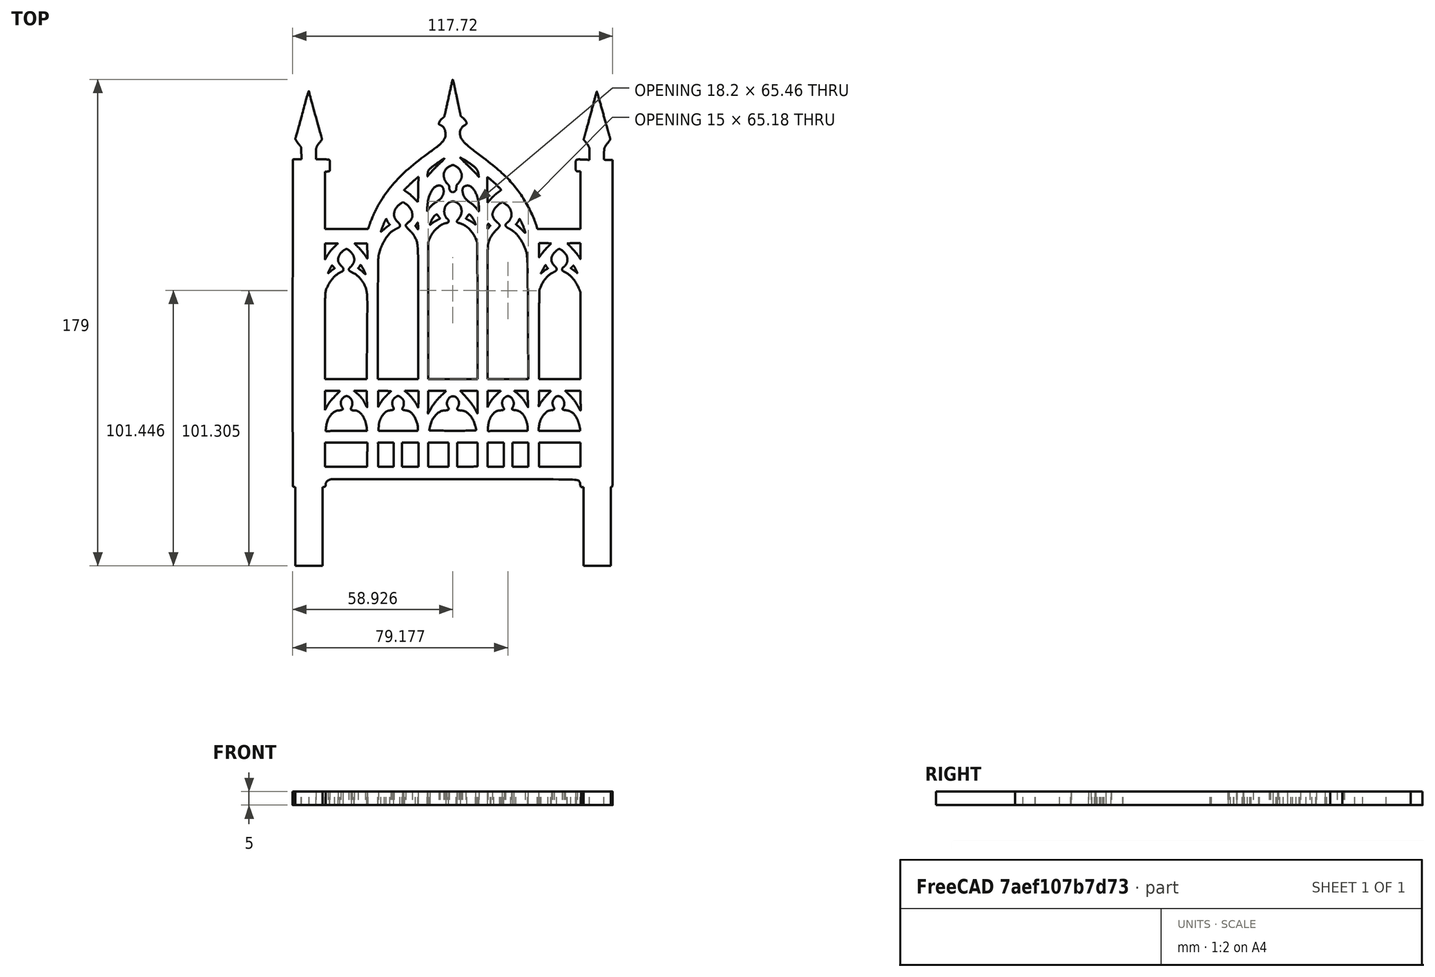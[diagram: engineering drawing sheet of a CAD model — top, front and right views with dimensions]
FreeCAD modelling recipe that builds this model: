
FCSTD DOCUMENT  (FreeCAD 1.0R1.0.1)
Label: Fence01_Flat
License: All rights reserved
LicenseURL: http://en.wikipedia.org/wiki/All_rights_reserved
objects: Part::Box×2, Sketcher::SketchObject×1, PartDesign::Pad×1, PartDesign::Body×1, Part::MultiFuse×1
note: 9 computed .brp shape members not serialized (recipe doc carries the construction recipe); baked Part::Feature solids carry a one-line shape summary decoded from their .brp

FEATURE [Sketcher::SketchObject] Sketch
  ArcFitTolerance = 1e-06
  AttachmentSupport = -> [XY_Plane]
  FullyConstrained = false
  MakeInternals = false
  MapMode = 5
  sketch-geometry (557):
    g0: BSplineCurve PolesCount=4 KnotsCount=2 Degree=3 IsPeriodic=0
    g1: BSplineCurve PolesCount=2 KnotsCount=2 Degree=1 IsPeriodic=0
    g2: BSplineCurve PolesCount=4 KnotsCount=2 Degree=3 IsPeriodic=0
    g3: BSplineCurve PolesCount=2 KnotsCount=2 Degree=1 IsPeriodic=0
    g4: BSplineCurve PolesCount=2 KnotsCount=2 Degree=1 IsPeriodic=0
    g5: BSplineCurve PolesCount=2 KnotsCount=2 Degree=1 IsPeriodic=0
    g6: BSplineCurve PolesCount=2 KnotsCount=2 Degree=1 IsPeriodic=0
    g7: BSplineCurve PolesCount=4 KnotsCount=2 Degree=3 IsPeriodic=0
    g8: BSplineCurve PolesCount=4 KnotsCount=2 Degree=3 IsPeriodic=0
    g9: BSplineCurve PolesCount=4 KnotsCount=2 Degree=3 IsPeriodic=0
    g10: BSplineCurve PolesCount=4 KnotsCount=2 Degree=3 IsPeriodic=0
    g11: BSplineCurve PolesCount=4 KnotsCount=2 Degree=3 IsPeriodic=0
    g12: BSplineCurve PolesCount=4 KnotsCount=2 Degree=3 IsPeriodic=0
    g13: BSplineCurve PolesCount=2 KnotsCount=2 Degree=1 IsPeriodic=0
    g14: BSplineCurve PolesCount=2 KnotsCount=2 Degree=1 IsPeriodic=0
    g15: BSplineCurve PolesCount=4 KnotsCount=2 Degree=3 IsPeriodic=0
    g16: BSplineCurve PolesCount=4 KnotsCount=2 Degree=3 IsPeriodic=0
    g17: BSplineCurve PolesCount=2 KnotsCount=2 Degree=1 IsPeriodic=0
    g18: BSplineCurve PolesCount=2 KnotsCount=2 Degree=1 IsPeriodic=0
    g19: BSplineCurve PolesCount=2 KnotsCount=2 Degree=1 IsPeriodic=0
    g20: BSplineCurve PolesCount=2 KnotsCount=2 Degree=1 IsPeriodic=0
    g21: BSplineCurve PolesCount=2 KnotsCount=2 Degree=1 IsPeriodic=0
    g22: BSplineCurve PolesCount=2 KnotsCount=2 Degree=1 IsPeriodic=0
    g23: BSplineCurve PolesCount=2 KnotsCount=2 Degree=1 IsPeriodic=0
    g24: BSplineCurve PolesCount=2 KnotsCount=2 Degree=1 IsPeriodic=0
    g25: BSplineCurve PolesCount=4 KnotsCount=2 Degree=3 IsPeriodic=0
    g26: BSplineCurve PolesCount=4 KnotsCount=2 Degree=3 IsPeriodic=0
    g27: BSplineCurve PolesCount=4 KnotsCount=2 Degree=3 IsPeriodic=0
    g28: BSplineCurve PolesCount=4 KnotsCount=2 Degree=3 IsPeriodic=0
    g29: BSplineCurve PolesCount=4 KnotsCount=2 Degree=3 IsPeriodic=0
    g30: BSplineCurve PolesCount=4 KnotsCount=2 Degree=3 IsPeriodic=0
    g31: BSplineCurve PolesCount=4 KnotsCount=2 Degree=3 IsPeriodic=0
    g32: BSplineCurve PolesCount=4 KnotsCount=2 Degree=3 IsPeriodic=0
    g33: BSplineCurve PolesCount=4 KnotsCount=2 Degree=3 IsPeriodic=0
    g34: BSplineCurve PolesCount=4 KnotsCount=2 Degree=3 IsPeriodic=0
    g35: BSplineCurve PolesCount=4 KnotsCount=2 Degree=3 IsPeriodic=0
    g36: BSplineCurve PolesCount=4 KnotsCount=2 Degree=3 IsPeriodic=0
    g37: BSplineCurve PolesCount=4 KnotsCount=2 Degree=3 IsPeriodic=0
    g38: BSplineCurve PolesCount=2 KnotsCount=2 Degree=1 IsPeriodic=0
    g39: BSplineCurve PolesCount=2 KnotsCount=2 Degree=1 IsPeriodic=0
    g40: BSplineCurve PolesCount=4 KnotsCount=2 Degree=3 IsPeriodic=0
    g41: BSplineCurve PolesCount=4 KnotsCount=2 Degree=3 IsPeriodic=0
    g42: BSplineCurve PolesCount=4 KnotsCount=2 Degree=3 IsPeriodic=0
    g43: BSplineCurve PolesCount=4 KnotsCount=2 Degree=3 IsPeriodic=0
    g44: BSplineCurve PolesCount=4 KnotsCount=2 Degree=3 IsPeriodic=0
    g45: BSplineCurve PolesCount=4 KnotsCount=2 Degree=3 IsPeriodic=0
    g46: BSplineCurve PolesCount=2 KnotsCount=2 Degree=1 IsPeriodic=0
    g47: BSplineCurve PolesCount=2 KnotsCount=2 Degree=1 IsPeriodic=0
    g48: BSplineCurve PolesCount=2 KnotsCount=2 Degree=1 IsPeriodic=0
    g49: BSplineCurve PolesCount=2 KnotsCount=2 Degree=1 IsPeriodic=0
    g50: BSplineCurve PolesCount=2 KnotsCount=2 Degree=1 IsPeriodic=0
    g51: BSplineCurve PolesCount=2 KnotsCount=2 Degree=1 IsPeriodic=0
    g52: BSplineCurve PolesCount=4 KnotsCount=2 Degree=3 IsPeriodic=0
    g53: BSplineCurve PolesCount=4 KnotsCount=2 Degree=3 IsPeriodic=0
    g54: BSplineCurve PolesCount=2 KnotsCount=2 Degree=1 IsPeriodic=0
    g55: BSplineCurve PolesCount=2 KnotsCount=2 Degree=1 IsPeriodic=0
    g56: BSplineCurve PolesCount=4 KnotsCount=2 Degree=3 IsPeriodic=0
    g57: BSplineCurve PolesCount=2 KnotsCount=2 Degree=1 IsPeriodic=0
    g58: BSplineCurve PolesCount=2 KnotsCount=2 Degree=1 IsPeriodic=0
    g59: BSplineCurve PolesCount=4 KnotsCount=2 Degree=3 IsPeriodic=0
    g60: BSplineCurve PolesCount=4 KnotsCount=2 Degree=3 IsPeriodic=0
    g61: BSplineCurve PolesCount=4 KnotsCount=2 Degree=3 IsPeriodic=0
    g62: BSplineCurve PolesCount=4 KnotsCount=2 Degree=3 IsPeriodic=0
    g63: BSplineCurve PolesCount=4 KnotsCount=2 Degree=3 IsPeriodic=0
    g64: BSplineCurve PolesCount=4 KnotsCount=2 Degree=3 IsPeriodic=0
    g65: BSplineCurve PolesCount=4 KnotsCount=2 Degree=3 IsPeriodic=0
    g66: BSplineCurve PolesCount=2 KnotsCount=2 Degree=1 IsPeriodic=0
    g67: BSplineCurve PolesCount=2 KnotsCount=2 Degree=1 IsPeriodic=0
    g68: BSplineCurve PolesCount=4 KnotsCount=2 Degree=3 IsPeriodic=0
    g69: BSplineCurve PolesCount=2 KnotsCount=2 Degree=1 IsPeriodic=0
    g70: BSplineCurve PolesCount=4 KnotsCount=2 Degree=3 IsPeriodic=0
    g71: BSplineCurve PolesCount=4 KnotsCount=2 Degree=3 IsPeriodic=0
    g72: BSplineCurve PolesCount=2 KnotsCount=2 Degree=1 IsPeriodic=0
    g73: BSplineCurve PolesCount=2 KnotsCount=2 Degree=1 IsPeriodic=0
    g74: BSplineCurve PolesCount=4 KnotsCount=2 Degree=3 IsPeriodic=0
    g75: BSplineCurve PolesCount=4 KnotsCount=2 Degree=3 IsPeriodic=0
    g76: BSplineCurve PolesCount=4 KnotsCount=2 Degree=3 IsPeriodic=0
    g77: BSplineCurve PolesCount=4 KnotsCount=2 Degree=3 IsPeriodic=0
    g78: BSplineCurve PolesCount=4 KnotsCount=2 Degree=3 IsPeriodic=0
    g79: BSplineCurve PolesCount=4 KnotsCount=2 Degree=3 IsPeriodic=0
    g80: BSplineCurve PolesCount=4 KnotsCount=2 Degree=3 IsPeriodic=0
    g81: BSplineCurve PolesCount=4 KnotsCount=2 Degree=3 IsPeriodic=0
    g82: BSplineCurve PolesCount=2 KnotsCount=2 Degree=1 IsPeriodic=0
    g83: BSplineCurve PolesCount=2 KnotsCount=2 Degree=1 IsPeriodic=0
    g84: BSplineCurve PolesCount=2 KnotsCount=2 Degree=1 IsPeriodic=0
    g85: BSplineCurve PolesCount=2 KnotsCount=2 Degree=1 IsPeriodic=0
    g86: BSplineCurve PolesCount=2 KnotsCount=2 Degree=1 IsPeriodic=0
    g87: BSplineCurve PolesCount=2 KnotsCount=2 Degree=1 IsPeriodic=0
    g88: BSplineCurve PolesCount=2 KnotsCount=2 Degree=1 IsPeriodic=0
    g89: BSplineCurve PolesCount=2 KnotsCount=2 Degree=1 IsPeriodic=0
    g90: BSplineCurve PolesCount=2 KnotsCount=2 Degree=1 IsPeriodic=0
    g91: BSplineCurve PolesCount=2 KnotsCount=2 Degree=1 IsPeriodic=0
    g92: BSplineCurve PolesCount=2 KnotsCount=2 Degree=1 IsPeriodic=0
    g93: BSplineCurve PolesCount=2 KnotsCount=2 Degree=1 IsPeriodic=0
    g94: BSplineCurve PolesCount=2 KnotsCount=2 Degree=1 IsPeriodic=0
    g95: BSplineCurve PolesCount=2 KnotsCount=2 Degree=1 IsPeriodic=0
    g96: BSplineCurve PolesCount=2 KnotsCount=2 Degree=1 IsPeriodic=0
    g97: BSplineCurve PolesCount=2 KnotsCount=2 Degree=1 IsPeriodic=0
    g98: BSplineCurve PolesCount=2 KnotsCount=2 Degree=1 IsPeriodic=0
    g99: BSplineCurve PolesCount=2 KnotsCount=2 Degree=1 IsPeriodic=0
    g100: BSplineCurve PolesCount=2 KnotsCount=2 Degree=1 IsPeriodic=0
    g101: BSplineCurve PolesCount=2 KnotsCount=2 Degree=1 IsPeriodic=0
    g102: BSplineCurve PolesCount=2 KnotsCount=2 Degree=1 IsPeriodic=0
    g103: BSplineCurve PolesCount=2 KnotsCount=2 Degree=1 IsPeriodic=0
    g104: BSplineCurve PolesCount=2 KnotsCount=2 Degree=1 IsPeriodic=0
    g105: BSplineCurve PolesCount=2 KnotsCount=2 Degree=1 IsPeriodic=0
    g106: BSplineCurve PolesCount=2 KnotsCount=2 Degree=1 IsPeriodic=0
    g107: BSplineCurve PolesCount=2 KnotsCount=2 Degree=1 IsPeriodic=0
    g108: BSplineCurve PolesCount=2 KnotsCount=2 Degree=1 IsPeriodic=0
    g109: BSplineCurve PolesCount=2 KnotsCount=2 Degree=1 IsPeriodic=0
    g110: BSplineCurve PolesCount=2 KnotsCount=2 Degree=1 IsPeriodic=0
    g111: BSplineCurve PolesCount=2 KnotsCount=2 Degree=1 IsPeriodic=0
    g112: BSplineCurve PolesCount=2 KnotsCount=2 Degree=1 IsPeriodic=0
    g113: BSplineCurve PolesCount=2 KnotsCount=2 Degree=1 IsPeriodic=0
    g114: BSplineCurve PolesCount=2 KnotsCount=2 Degree=1 IsPeriodic=0
    g115: BSplineCurve PolesCount=4 KnotsCount=2 Degree=3 IsPeriodic=0
    g116: BSplineCurve PolesCount=2 KnotsCount=2 Degree=1 IsPeriodic=0
    g117: BSplineCurve PolesCount=2 KnotsCount=2 Degree=1 IsPeriodic=0
    g118: BSplineCurve PolesCount=2 KnotsCount=2 Degree=1 IsPeriodic=0
    g119: BSplineCurve PolesCount=2 KnotsCount=2 Degree=1 IsPeriodic=0
    g120: BSplineCurve PolesCount=2 KnotsCount=2 Degree=1 IsPeriodic=0
    g121: BSplineCurve PolesCount=2 KnotsCount=2 Degree=1 IsPeriodic=0
    g122: BSplineCurve PolesCount=4 KnotsCount=2 Degree=3 IsPeriodic=0
    g123: BSplineCurve PolesCount=2 KnotsCount=2 Degree=1 IsPeriodic=0
    g124: BSplineCurve PolesCount=2 KnotsCount=2 Degree=1 IsPeriodic=0
    g125: BSplineCurve PolesCount=2 KnotsCount=2 Degree=1 IsPeriodic=0
    g126: BSplineCurve PolesCount=2 KnotsCount=2 Degree=1 IsPeriodic=0
    g127: BSplineCurve PolesCount=2 KnotsCount=2 Degree=1 IsPeriodic=0
    g128: BSplineCurve PolesCount=2 KnotsCount=2 Degree=1 IsPeriodic=0
    g129: BSplineCurve PolesCount=2 KnotsCount=2 Degree=1 IsPeriodic=0
    g130: BSplineCurve PolesCount=2 KnotsCount=2 Degree=1 IsPeriodic=0
    g131: BSplineCurve PolesCount=2 KnotsCount=2 Degree=1 IsPeriodic=0
    g132: BSplineCurve PolesCount=2 KnotsCount=2 Degree=1 IsPeriodic=0
    g133: BSplineCurve PolesCount=2 KnotsCount=2 Degree=1 IsPeriodic=0
    g134: BSplineCurve PolesCount=2 KnotsCount=2 Degree=1 IsPeriodic=0
    g135: BSplineCurve PolesCount=2 KnotsCount=2 Degree=1 IsPeriodic=0
    g136: BSplineCurve PolesCount=2 KnotsCount=2 Degree=1 IsPeriodic=0
    g137: BSplineCurve PolesCount=2 KnotsCount=2 Degree=1 IsPeriodic=0
    g138: BSplineCurve PolesCount=2 KnotsCount=2 Degree=1 IsPeriodic=0
    g139: BSplineCurve PolesCount=2 KnotsCount=2 Degree=1 IsPeriodic=0
    g140: BSplineCurve PolesCount=2 KnotsCount=2 Degree=1 IsPeriodic=0
    g141: BSplineCurve PolesCount=2 KnotsCount=2 Degree=1 IsPeriodic=0
    g142: BSplineCurve PolesCount=2 KnotsCount=2 Degree=1 IsPeriodic=0
    g143: BSplineCurve PolesCount=2 KnotsCount=2 Degree=1 IsPeriodic=0
    g144: BSplineCurve PolesCount=2 KnotsCount=2 Degree=1 IsPeriodic=0
    g145: BSplineCurve PolesCount=2 KnotsCount=2 Degree=1 IsPeriodic=0
    g146: BSplineCurve PolesCount=2 KnotsCount=2 Degree=1 IsPeriodic=0
    g147: BSplineCurve PolesCount=2 KnotsCount=2 Degree=1 IsPeriodic=0
    g148: BSplineCurve PolesCount=2 KnotsCount=2 Degree=1 IsPeriodic=0
    g149: BSplineCurve PolesCount=4 KnotsCount=2 Degree=3 IsPeriodic=0
    g150: BSplineCurve PolesCount=4 KnotsCount=2 Degree=3 IsPeriodic=0
    g151: BSplineCurve PolesCount=4 KnotsCount=2 Degree=3 IsPeriodic=0
    g152: BSplineCurve PolesCount=4 KnotsCount=2 Degree=3 IsPeriodic=0
    g153: BSplineCurve PolesCount=4 KnotsCount=2 Degree=3 IsPeriodic=0
    g154: BSplineCurve PolesCount=4 KnotsCount=2 Degree=3 IsPeriodic=0
    g155: BSplineCurve PolesCount=4 KnotsCount=2 Degree=3 IsPeriodic=0
    g156: BSplineCurve PolesCount=4 KnotsCount=2 Degree=3 IsPeriodic=0
    g157: BSplineCurve PolesCount=4 KnotsCount=2 Degree=3 IsPeriodic=0
    g158: BSplineCurve PolesCount=2 KnotsCount=2 Degree=1 IsPeriodic=0
    g159: BSplineCurve PolesCount=2 KnotsCount=2 Degree=1 IsPeriodic=0
    g160: BSplineCurve PolesCount=4 KnotsCount=2 Degree=3 IsPeriodic=0
    g161: BSplineCurve PolesCount=2 KnotsCount=2 Degree=1 IsPeriodic=0
    g162: BSplineCurve PolesCount=4 KnotsCount=2 Degree=3 IsPeriodic=0
    g163: BSplineCurve PolesCount=4 KnotsCount=2 Degree=3 IsPeriodic=0
    g164: BSplineCurve PolesCount=4 KnotsCount=2 Degree=3 IsPeriodic=0
    g165: BSplineCurve PolesCount=4 KnotsCount=2 Degree=3 IsPeriodic=0
    g166: BSplineCurve PolesCount=4 KnotsCount=2 Degree=3 IsPeriodic=0
    g167: BSplineCurve PolesCount=4 KnotsCount=2 Degree=3 IsPeriodic=0
    g168: BSplineCurve PolesCount=4 KnotsCount=2 Degree=3 IsPeriodic=0
    g169: BSplineCurve PolesCount=4 KnotsCount=2 Degree=3 IsPeriodic=0
    g170: BSplineCurve PolesCount=4 KnotsCount=2 Degree=3 IsPeriodic=0
    g171: BSplineCurve PolesCount=4 KnotsCount=2 Degree=3 IsPeriodic=0
    g172: BSplineCurve PolesCount=4 KnotsCount=2 Degree=3 IsPeriodic=0
    g173: BSplineCurve PolesCount=4 KnotsCount=2 Degree=3 IsPeriodic=0
    g174: BSplineCurve PolesCount=4 KnotsCount=2 Degree=3 IsPeriodic=0
    g175: BSplineCurve PolesCount=4 KnotsCount=2 Degree=3 IsPeriodic=0
    g176: BSplineCurve PolesCount=2 KnotsCount=2 Degree=1 IsPeriodic=0
    g177: BSplineCurve PolesCount=2 KnotsCount=2 Degree=1 IsPeriodic=0
    g178: BSplineCurve PolesCount=2 KnotsCount=2 Degree=1 IsPeriodic=0
    g179: BSplineCurve PolesCount=2 KnotsCount=2 Degree=1 IsPeriodic=0
    g180: BSplineCurve PolesCount=4 KnotsCount=2 Degree=3 IsPeriodic=0
    g181: BSplineCurve PolesCount=4 KnotsCount=2 Degree=3 IsPeriodic=0
    g182: BSplineCurve PolesCount=4 KnotsCount=2 Degree=3 IsPeriodic=0
    g183: BSplineCurve PolesCount=4 KnotsCount=2 Degree=3 IsPeriodic=0
    g184: BSplineCurve PolesCount=4 KnotsCount=2 Degree=3 IsPeriodic=0
    g185: BSplineCurve PolesCount=4 KnotsCount=2 Degree=3 IsPeriodic=0
    g186: BSplineCurve PolesCount=4 KnotsCount=2 Degree=3 IsPeriodic=0
    g187: BSplineCurve PolesCount=4 KnotsCount=2 Degree=3 IsPeriodic=0
    g188: BSplineCurve PolesCount=4 KnotsCount=2 Degree=3 IsPeriodic=0
    g189: BSplineCurve PolesCount=4 KnotsCount=2 Degree=3 IsPeriodic=0
    g190: BSplineCurve PolesCount=4 KnotsCount=2 Degree=3 IsPeriodic=0
    g191: BSplineCurve PolesCount=4 KnotsCount=2 Degree=3 IsPeriodic=0
    g192: BSplineCurve PolesCount=4 KnotsCount=2 Degree=3 IsPeriodic=0
    g193: BSplineCurve PolesCount=2 KnotsCount=2 Degree=1 IsPeriodic=0
    g194: BSplineCurve PolesCount=4 KnotsCount=2 Degree=3 IsPeriodic=0
    g195: BSplineCurve PolesCount=4 KnotsCount=2 Degree=3 IsPeriodic=0
    g196: BSplineCurve PolesCount=4 KnotsCount=2 Degree=3 IsPeriodic=0
    g197: BSplineCurve PolesCount=4 KnotsCount=2 Degree=3 IsPeriodic=0
    g198: BSplineCurve PolesCount=4 KnotsCount=2 Degree=3 IsPeriodic=0
    g199: BSplineCurve PolesCount=4 KnotsCount=2 Degree=3 IsPeriodic=0
    g200: BSplineCurve PolesCount=4 KnotsCount=2 Degree=3 IsPeriodic=0
    g201: BSplineCurve PolesCount=4 KnotsCount=2 Degree=3 IsPeriodic=0
    g202: BSplineCurve PolesCount=4 KnotsCount=2 Degree=3 IsPeriodic=0
    g203: BSplineCurve PolesCount=4 KnotsCount=2 Degree=3 IsPeriodic=0
    g204: BSplineCurve PolesCount=4 KnotsCount=2 Degree=3 IsPeriodic=0
    g205: BSplineCurve PolesCount=4 KnotsCount=2 Degree=3 IsPeriodic=0
    g206: BSplineCurve PolesCount=4 KnotsCount=2 Degree=3 IsPeriodic=0
    g207: BSplineCurve PolesCount=4 KnotsCount=2 Degree=3 IsPeriodic=0
    g208: BSplineCurve PolesCount=4 KnotsCount=2 Degree=3 IsPeriodic=0
    g209: BSplineCurve PolesCount=4 KnotsCount=2 Degree=3 IsPeriodic=0
    g210: BSplineCurve PolesCount=4 KnotsCount=2 Degree=3 IsPeriodic=0
    g211: BSplineCurve PolesCount=4 KnotsCount=2 Degree=3 IsPeriodic=0
    g212: BSplineCurve PolesCount=4 KnotsCount=2 Degree=3 IsPeriodic=0
    g213: BSplineCurve PolesCount=4 KnotsCount=2 Degree=3 IsPeriodic=0
    g214: BSplineCurve PolesCount=4 KnotsCount=2 Degree=3 IsPeriodic=0
    g215: BSplineCurve PolesCount=4 KnotsCount=2 Degree=3 IsPeriodic=0
    g216: BSplineCurve PolesCount=2 KnotsCount=2 Degree=1 IsPeriodic=0
    g217: BSplineCurve PolesCount=2 KnotsCount=2 Degree=1 IsPeriodic=0
    g218: BSplineCurve PolesCount=2 KnotsCount=2 Degree=1 IsPeriodic=0
    g219: BSplineCurve PolesCount=2 KnotsCount=2 Degree=1 IsPeriodic=0
    g220: BSplineCurve PolesCount=4 KnotsCount=2 Degree=3 IsPeriodic=0
    g221: BSplineCurve PolesCount=2 KnotsCount=2 Degree=1 IsPeriodic=0
    g222: BSplineCurve PolesCount=2 KnotsCount=2 Degree=1 IsPeriodic=0
    g223: BSplineCurve PolesCount=2 KnotsCount=2 Degree=1 IsPeriodic=0
    g224: BSplineCurve PolesCount=2 KnotsCount=2 Degree=1 IsPeriodic=0
    g225: BSplineCurve PolesCount=4 KnotsCount=2 Degree=3 IsPeriodic=0
    g226: BSplineCurve PolesCount=4 KnotsCount=2 Degree=3 IsPeriodic=0
    g227: BSplineCurve PolesCount=4 KnotsCount=2 Degree=3 IsPeriodic=0
    g228: BSplineCurve PolesCount=2 KnotsCount=2 Degree=1 IsPeriodic=0
    g229: BSplineCurve PolesCount=2 KnotsCount=2 Degree=1 IsPeriodic=0
    g230: BSplineCurve PolesCount=2 KnotsCount=2 Degree=1 IsPeriodic=0
    g231: BSplineCurve PolesCount=4 KnotsCount=2 Degree=3 IsPeriodic=0
    g232: BSplineCurve PolesCount=4 KnotsCount=2 Degree=3 IsPeriodic=0
    g233: BSplineCurve PolesCount=4 KnotsCount=2 Degree=3 IsPeriodic=0
    g234: BSplineCurve PolesCount=4 KnotsCount=2 Degree=3 IsPeriodic=0
    g235: BSplineCurve PolesCount=4 KnotsCount=2 Degree=3 IsPeriodic=0
    g236: BSplineCurve PolesCount=2 KnotsCount=2 Degree=1 IsPeriodic=0
    g237: BSplineCurve PolesCount=2 KnotsCount=2 Degree=1 IsPeriodic=0
    g238: BSplineCurve PolesCount=2 KnotsCount=2 Degree=1 IsPeriodic=0
    g239: BSplineCurve PolesCount=4 KnotsCount=2 Degree=3 IsPeriodic=0
    g240: BSplineCurve PolesCount=4 KnotsCount=2 Degree=3 IsPeriodic=0
    g241: BSplineCurve PolesCount=4 KnotsCount=2 Degree=3 IsPeriodic=0
    g242: BSplineCurve PolesCount=4 KnotsCount=2 Degree=3 IsPeriodic=0
    g243: BSplineCurve PolesCount=4 KnotsCount=2 Degree=3 IsPeriodic=0
    g244: BSplineCurve PolesCount=2 KnotsCount=2 Degree=1 IsPeriodic=0
    g245: BSplineCurve PolesCount=4 KnotsCount=2 Degree=3 IsPeriodic=0
    g246: BSplineCurve PolesCount=2 KnotsCount=2 Degree=1 IsPeriodic=0
    g247: BSplineCurve PolesCount=2 KnotsCount=2 Degree=1 IsPeriodic=0
    g248: BSplineCurve PolesCount=2 KnotsCount=2 Degree=1 IsPeriodic=0
    g249: BSplineCurve PolesCount=2 KnotsCount=2 Degree=1 IsPeriodic=0
    g250: BSplineCurve PolesCount=2 KnotsCount=2 Degree=1 IsPeriodic=0
    g251: BSplineCurve PolesCount=2 KnotsCount=2 Degree=1 IsPeriodic=0
    g252: BSplineCurve PolesCount=4 KnotsCount=2 Degree=3 IsPeriodic=0
    g253: BSplineCurve PolesCount=2 KnotsCount=2 Degree=1 IsPeriodic=0
    g254: BSplineCurve PolesCount=2 KnotsCount=2 Degree=1 IsPeriodic=0
    g255: BSplineCurve PolesCount=2 KnotsCount=2 Degree=1 IsPeriodic=0
    g256: BSplineCurve PolesCount=2 KnotsCount=2 Degree=1 IsPeriodic=0
    g257: BSplineCurve PolesCount=2 KnotsCount=2 Degree=1 IsPeriodic=0
    g258: BSplineCurve PolesCount=4 KnotsCount=2 Degree=3 IsPeriodic=0
    g259: BSplineCurve PolesCount=4 KnotsCount=2 Degree=3 IsPeriodic=0
    g260: BSplineCurve PolesCount=4 KnotsCount=2 Degree=3 IsPeriodic=0
    g261: BSplineCurve PolesCount=2 KnotsCount=2 Degree=1 IsPeriodic=0
    g262: BSplineCurve PolesCount=4 KnotsCount=2 Degree=3 IsPeriodic=0
    g263: BSplineCurve PolesCount=2 KnotsCount=2 Degree=1 IsPeriodic=0
    g264: BSplineCurve PolesCount=2 KnotsCount=2 Degree=1 IsPeriodic=0
    g265: BSplineCurve PolesCount=2 KnotsCount=2 Degree=1 IsPeriodic=0
    g266: BSplineCurve PolesCount=2 KnotsCount=2 Degree=1 IsPeriodic=0
    g267: BSplineCurve PolesCount=4 KnotsCount=2 Degree=3 IsPeriodic=0
    g268: BSplineCurve PolesCount=4 KnotsCount=2 Degree=3 IsPeriodic=0
    g269: BSplineCurve PolesCount=4 KnotsCount=2 Degree=3 IsPeriodic=0
    g270: BSplineCurve PolesCount=4 KnotsCount=2 Degree=3 IsPeriodic=0
    g271: BSplineCurve PolesCount=2 KnotsCount=2 Degree=1 IsPeriodic=0
    g272: BSplineCurve PolesCount=4 KnotsCount=2 Degree=3 IsPeriodic=0
    g273: BSplineCurve PolesCount=2 KnotsCount=2 Degree=1 IsPeriodic=0
    g274: BSplineCurve PolesCount=2 KnotsCount=2 Degree=1 IsPeriodic=0
    g275: BSplineCurve PolesCount=2 KnotsCount=2 Degree=1 IsPeriodic=0
    g276: BSplineCurve PolesCount=2 KnotsCount=2 Degree=1 IsPeriodic=0
    g277: BSplineCurve PolesCount=2 KnotsCount=2 Degree=1 IsPeriodic=0
    g278: BSplineCurve PolesCount=2 KnotsCount=2 Degree=1 IsPeriodic=0
    g279: BSplineCurve PolesCount=4 KnotsCount=2 Degree=3 IsPeriodic=0
    g280: BSplineCurve PolesCount=2 KnotsCount=2 Degree=1 IsPeriodic=0
    g281: BSplineCurve PolesCount=4 KnotsCount=2 Degree=3 IsPeriodic=0
    g282: BSplineCurve PolesCount=2 KnotsCount=2 Degree=1 IsPeriodic=0
    g283: BSplineCurve PolesCount=2 KnotsCount=2 Degree=1 IsPeriodic=0
    g284: BSplineCurve PolesCount=2 KnotsCount=2 Degree=1 IsPeriodic=0
    g285: BSplineCurve PolesCount=2 KnotsCount=2 Degree=1 IsPeriodic=0
    g286: BSplineCurve PolesCount=4 KnotsCount=2 Degree=3 IsPeriodic=0
    g287: BSplineCurve PolesCount=4 KnotsCount=2 Degree=3 IsPeriodic=0
    g288: BSplineCurve PolesCount=4 KnotsCount=2 Degree=3 IsPeriodic=0
    g289: BSplineCurve PolesCount=2 KnotsCount=2 Degree=1 IsPeriodic=0
    g290: BSplineCurve PolesCount=4 KnotsCount=2 Degree=3 IsPeriodic=0
    g291: BSplineCurve PolesCount=4 KnotsCount=2 Degree=3 IsPeriodic=0
    g292: BSplineCurve PolesCount=4 KnotsCount=2 Degree=3 IsPeriodic=0
    g293: BSplineCurve PolesCount=2 KnotsCount=2 Degree=1 IsPeriodic=0
    g294: BSplineCurve PolesCount=2 KnotsCount=2 Degree=1 IsPeriodic=0
    g295: BSplineCurve PolesCount=2 KnotsCount=2 Degree=1 IsPeriodic=0
    g296: BSplineCurve PolesCount=2 KnotsCount=2 Degree=1 IsPeriodic=0
    g297: BSplineCurve PolesCount=4 KnotsCount=2 Degree=3 IsPeriodic=0
    g298: BSplineCurve PolesCount=2 KnotsCount=2 Degree=1 IsPeriodic=0
    g299: BSplineCurve PolesCount=4 KnotsCount=2 Degree=3 IsPeriodic=0
    g300: BSplineCurve PolesCount=2 KnotsCount=2 Degree=1 IsPeriodic=0
    g301: BSplineCurve PolesCount=2 KnotsCount=2 Degree=1 IsPeriodic=0
    g302: BSplineCurve PolesCount=2 KnotsCount=2 Degree=1 IsPeriodic=0
    g303: BSplineCurve PolesCount=2 KnotsCount=2 Degree=1 IsPeriodic=0
    g304: BSplineCurve PolesCount=4 KnotsCount=2 Degree=3 IsPeriodic=0
    g305: BSplineCurve PolesCount=4 KnotsCount=2 Degree=3 IsPeriodic=0
    g306: BSplineCurve PolesCount=4 KnotsCount=2 Degree=3 IsPeriodic=0
    g307: BSplineCurve PolesCount=2 KnotsCount=2 Degree=1 IsPeriodic=0
    g308: BSplineCurve PolesCount=4 KnotsCount=2 Degree=3 IsPeriodic=0
    g309: BSplineCurve PolesCount=4 KnotsCount=2 Degree=3 IsPeriodic=0
    g310: BSplineCurve PolesCount=4 KnotsCount=2 Degree=3 IsPeriodic=0
    g311: BSplineCurve PolesCount=4 KnotsCount=2 Degree=3 IsPeriodic=0
    g312: BSplineCurve PolesCount=4 KnotsCount=2 Degree=3 IsPeriodic=0
    g313: BSplineCurve PolesCount=4 KnotsCount=2 Degree=3 IsPeriodic=0
    g314: BSplineCurve PolesCount=4 KnotsCount=2 Degree=3 IsPeriodic=0
    g315: BSplineCurve PolesCount=4 KnotsCount=2 Degree=3 IsPeriodic=0
    g316: BSplineCurve PolesCount=4 KnotsCount=2 Degree=3 IsPeriodic=0
    g317: BSplineCurve PolesCount=4 KnotsCount=2 Degree=3 IsPeriodic=0
    g318: BSplineCurve PolesCount=4 KnotsCount=2 Degree=3 IsPeriodic=0
    g319: BSplineCurve PolesCount=4 KnotsCount=2 Degree=3 IsPeriodic=0
    g320: BSplineCurve PolesCount=4 KnotsCount=2 Degree=3 IsPeriodic=0
    g321: BSplineCurve PolesCount=2 KnotsCount=2 Degree=1 IsPeriodic=0
    g322: BSplineCurve PolesCount=2 KnotsCount=2 Degree=1 IsPeriodic=0
    g323: BSplineCurve PolesCount=2 KnotsCount=2 Degree=1 IsPeriodic=0
    g324: BSplineCurve PolesCount=2 KnotsCount=2 Degree=1 IsPeriodic=0
    g325: BSplineCurve PolesCount=4 KnotsCount=2 Degree=3 IsPeriodic=0
    g326: BSplineCurve PolesCount=4 KnotsCount=2 Degree=3 IsPeriodic=0
    g327: BSplineCurve PolesCount=4 KnotsCount=2 Degree=3 IsPeriodic=0
    g328: BSplineCurve PolesCount=4 KnotsCount=2 Degree=3 IsPeriodic=0
    g329: BSplineCurve PolesCount=4 KnotsCount=2 Degree=3 IsPeriodic=0
    g330: BSplineCurve PolesCount=2 KnotsCount=2 Degree=1 IsPeriodic=0
    g331: BSplineCurve PolesCount=2 KnotsCount=2 Degree=1 IsPeriodic=0
    g332: BSplineCurve PolesCount=4 KnotsCount=2 Degree=3 IsPeriodic=0
    g333: BSplineCurve PolesCount=4 KnotsCount=2 Degree=3 IsPeriodic=0
    g334: BSplineCurve PolesCount=4 KnotsCount=2 Degree=3 IsPeriodic=0
    g335: BSplineCurve PolesCount=4 KnotsCount=2 Degree=3 IsPeriodic=0
    g336: BSplineCurve PolesCount=4 KnotsCount=2 Degree=3 IsPeriodic=0
    g337: BSplineCurve PolesCount=4 KnotsCount=2 Degree=3 IsPeriodic=0
    g338: BSplineCurve PolesCount=4 KnotsCount=2 Degree=3 IsPeriodic=0
    g339: BSplineCurve PolesCount=2 KnotsCount=2 Degree=1 IsPeriodic=0
    g340: BSplineCurve PolesCount=2 KnotsCount=2 Degree=1 IsPeriodic=0
    g341: BSplineCurve PolesCount=2 KnotsCount=2 Degree=1 IsPeriodic=0
    g342: BSplineCurve PolesCount=2 KnotsCount=2 Degree=1 IsPeriodic=0
    g343: BSplineCurve PolesCount=2 KnotsCount=2 Degree=1 IsPeriodic=0
    g344: BSplineCurve PolesCount=2 KnotsCount=2 Degree=1 IsPeriodic=0
    g345: BSplineCurve PolesCount=4 KnotsCount=2 Degree=3 IsPeriodic=0
    g346: BSplineCurve PolesCount=4 KnotsCount=2 Degree=3 IsPeriodic=0
    g347: BSplineCurve PolesCount=4 KnotsCount=2 Degree=3 IsPeriodic=0
    g348: BSplineCurve PolesCount=4 KnotsCount=2 Degree=3 IsPeriodic=0
    g349: BSplineCurve PolesCount=4 KnotsCount=2 Degree=3 IsPeriodic=0
    g350: BSplineCurve PolesCount=4 KnotsCount=2 Degree=3 IsPeriodic=0
    g351: BSplineCurve PolesCount=4 KnotsCount=2 Degree=3 IsPeriodic=0
    g352: BSplineCurve PolesCount=4 KnotsCount=2 Degree=3 IsPeriodic=0
    g353: BSplineCurve PolesCount=4 KnotsCount=2 Degree=3 IsPeriodic=0
    g354: BSplineCurve PolesCount=4 KnotsCount=2 Degree=3 IsPeriodic=0
    g355: BSplineCurve PolesCount=2 KnotsCount=2 Degree=1 IsPeriodic=0
    g356: BSplineCurve PolesCount=2 KnotsCount=2 Degree=1 IsPeriodic=0
    g357: BSplineCurve PolesCount=4 KnotsCount=2 Degree=3 IsPeriodic=0
    g358: BSplineCurve PolesCount=2 KnotsCount=2 Degree=1 IsPeriodic=0
    g359: BSplineCurve PolesCount=2 KnotsCount=2 Degree=1 IsPeriodic=0
    g360: BSplineCurve PolesCount=2 KnotsCount=2 Degree=1 IsPeriodic=0
    g361: BSplineCurve PolesCount=2 KnotsCount=2 Degree=1 IsPeriodic=0
    g362: BSplineCurve PolesCount=4 KnotsCount=2 Degree=3 IsPeriodic=0
    g363: BSplineCurve PolesCount=4 KnotsCount=2 Degree=3 IsPeriodic=0
    g364: BSplineCurve PolesCount=4 KnotsCount=2 Degree=3 IsPeriodic=0
    g365: BSplineCurve PolesCount=4 KnotsCount=2 Degree=3 IsPeriodic=0
    g366: BSplineCurve PolesCount=4 KnotsCount=2 Degree=3 IsPeriodic=0
    g367: BSplineCurve PolesCount=4 KnotsCount=2 Degree=3 IsPeriodic=0
    g368: BSplineCurve PolesCount=4 KnotsCount=2 Degree=3 IsPeriodic=0
    g369: BSplineCurve PolesCount=2 KnotsCount=2 Degree=1 IsPeriodic=0
    g370: BSplineCurve PolesCount=2 KnotsCount=2 Degree=1 IsPeriodic=0
    g371: BSplineCurve PolesCount=4 KnotsCount=2 Degree=3 IsPeriodic=0
    g372: BSplineCurve PolesCount=4 KnotsCount=2 Degree=3 IsPeriodic=0
    g373: BSplineCurve PolesCount=4 KnotsCount=2 Degree=3 IsPeriodic=0
    g374: BSplineCurve PolesCount=4 KnotsCount=2 Degree=3 IsPeriodic=0
    g375: BSplineCurve PolesCount=4 KnotsCount=2 Degree=3 IsPeriodic=0
    g376: BSplineCurve PolesCount=4 KnotsCount=2 Degree=3 IsPeriodic=0
    g377: BSplineCurve PolesCount=2 KnotsCount=2 Degree=1 IsPeriodic=0
    g378: BSplineCurve PolesCount=2 KnotsCount=2 Degree=1 IsPeriodic=0
    g379: BSplineCurve PolesCount=2 KnotsCount=2 Degree=1 IsPeriodic=0
    g380: BSplineCurve PolesCount=2 KnotsCount=2 Degree=1 IsPeriodic=0
    g381: BSplineCurve PolesCount=2 KnotsCount=2 Degree=1 IsPeriodic=0
    g382: BSplineCurve PolesCount=2 KnotsCount=2 Degree=1 IsPeriodic=0
    g383: BSplineCurve PolesCount=4 KnotsCount=2 Degree=3 IsPeriodic=0
    g384: BSplineCurve PolesCount=4 KnotsCount=2 Degree=3 IsPeriodic=0
    g385: BSplineCurve PolesCount=4 KnotsCount=2 Degree=3 IsPeriodic=0
    g386: BSplineCurve PolesCount=4 KnotsCount=2 Degree=3 IsPeriodic=0
    g387: BSplineCurve PolesCount=4 KnotsCount=2 Degree=3 IsPeriodic=0
    g388: BSplineCurve PolesCount=4 KnotsCount=2 Degree=3 IsPeriodic=0
    g389: BSplineCurve PolesCount=4 KnotsCount=2 Degree=3 IsPeriodic=0
    g390: BSplineCurve PolesCount=4 KnotsCount=2 Degree=3 IsPeriodic=0
    g391: BSplineCurve PolesCount=4 KnotsCount=2 Degree=3 IsPeriodic=0
    g392: BSplineCurve PolesCount=4 KnotsCount=2 Degree=3 IsPeriodic=0
    g393: BSplineCurve PolesCount=4 KnotsCount=2 Degree=3 IsPeriodic=0
    g394: BSplineCurve PolesCount=2 KnotsCount=2 Degree=1 IsPeriodic=0
    g395: BSplineCurve PolesCount=2 KnotsCount=2 Degree=1 IsPeriodic=0
    g396: BSplineCurve PolesCount=2 KnotsCount=2 Degree=1 IsPeriodic=0
    g397: BSplineCurve PolesCount=2 KnotsCount=2 Degree=1 IsPeriodic=0
    g398: BSplineCurve PolesCount=2 KnotsCount=2 Degree=1 IsPeriodic=0
    g399: BSplineCurve PolesCount=2 KnotsCount=2 Degree=1 IsPeriodic=0
    ... +157 more geometry lines
  constraints (557):
    c: Coincident(g0,g1)
    c: Coincident(g1,g2)
    c: Coincident(g2,g3)
    c: Coincident(g3,g4)
    c: Coincident(g4,g5)
    c: Coincident(g5,g6)
    c: Coincident(g6,g7)
    c: Coincident(g7,g8)
    c: Coincident(g8,g9)
    c: Coincident(g9,g10)
    c: Coincident(g10,g11)
    c: Coincident(g11,g12)
    c: Coincident(g12,g13)
    c: Coincident(g13,g14)
    c: Coincident(g14,g15)
    c: Coincident(g15,g16)
    c: Coincident(g16,g17)
    c: Coincident(g17,g18)
    c: Coincident(g18,g19)
    c: Coincident(g19,g20)
    c: Coincident(g20,g21)
    c: Coincident(g21,g22)
    c: Coincident(g22,g23)
    c: Coincident(g23,g24)
    c: Coincident(g24,g25)
    c: Coincident(g25,g26)
    c: Coincident(g26,g27)
    c: Coincident(g27,g28)
    c: Coincident(g28,g29)
    c: Coincident(g29,g30)
    c: Coincident(g30,g31)
    c: Coincident(g31,g32)
    c: Coincident(g32,g33)
    c: Coincident(g33,g34)
    c: Coincident(g34,g35)
    c: Coincident(g35,g36)
    c: Coincident(g36,g37)
    c: Coincident(g37,g38)
    c: Coincident(g38,g39)
    c: Coincident(g39,g40)
    c: Coincident(g40,g41)
    c: Coincident(g41,g42)
    c: Coincident(g42,g43)
    c: Coincident(g43,g44)
    c: Coincident(g44,g45)
    c: Coincident(g45,g46)
    c: Coincident(g46,g47)
    c: Coincident(g47,g48)
    c: Coincident(g48,g49)
    c: Coincident(g49,g50)
    c: Coincident(g50,g51)
    c: Coincident(g51,g52)
    c: Coincident(g52,g53)
    c: Coincident(g53,g54)
    c: Coincident(g54,g55)
    c: Coincident(g55,g56)
    c: Coincident(g56,g57)
    c: Coincident(g57,g58)
    c: Coincident(g58,g59)
    c: Coincident(g59,g60)
    c: Coincident(g60,g61)
    c: Coincident(g61,g62)
    c: Coincident(g62,g63)
    c: Coincident(g63,g64)
    c: Coincident(g64,g65)
    c: Coincident(g65,g66)
    c: Coincident(g66,g67)
    c: Coincident(g67,g68)
    c: Coincident(g68,g69)
    c: Coincident(g69,g70)
    c: Coincident(g70,g71)
    c: Coincident(g71,g72)
    c: Coincident(g72,g73)
    c: Coincident(g73,g74)
    c: Coincident(g74,g75)
    c: Coincident(g75,g76)
    c: Coincident(g76,g77)
    c: Coincident(g77,g78)
    c: Coincident(g78,g79)
    c: Coincident(g79,g80)
    c: Coincident(g80,g81)
    c: Coincident(g81,g82)
    c: Coincident(g82,g0)
    c: Coincident(g83,g84)
    c: Coincident(g84,g85)
    c: Coincident(g85,g86)
    c: Coincident(g86,g87)
    c: Coincident(g87,g88)
    c: Coincident(g88,g89)
    c: Coincident(g89,g90)
    c: Coincident(g90,g83)
    c: Coincident(g91,g92)
    c: Coincident(g92,g93)
    c: Coincident(g93,g94)
    c: Coincident(g94,g95)
    c: Coincident(g95,g96)
    c: Coincident(g96,g97)
    c: Coincident(g97,g98)
    c: Coincident(g98,g91)
    c: Coincident(g99,g100)
    c: Coincident(g100,g101)
    c: Coincident(g101,g102)
    c: Coincident(g102,g103)
    c: Coincident(g103,g104)
    c: Coincident(g104,g105)
    c: Coincident(g105,g106)
    c: Coincident(g106,g99)
    c: Coincident(g107,g108)
    c: Coincident(g108,g109)
    c: Coincident(g109,g110)
    c: Coincident(g110,g111)
    c: Coincident(g111,g112)
    c: Coincident(g112,g113)
    c: Coincident(g113,g114)
    c: Coincident(g114,g107)
    c: Coincident(g115,g116)
    c: Coincident(g116,g117)
    c: Coincident(g117,g118)
    c: Coincident(g118,g119)
    c: Coincident(g119,g120)
    c: Coincident(g120,g121)
    c: Coincident(g121,g122)
    c: Coincident(g122,g115)
    c: Coincident(g123,g124)
    c: Coincident(g124,g125)
    c: Coincident(g125,g126)
    c: Coincident(g126,g127)
    c: Coincident(g127,g128)
    c: Coincident(g128,g129)
    c: Coincident(g129,g130)
    c: Coincident(g130,g123)
    c: Coincident(g131,g132)
    c: Coincident(g132,g133)
    c: Coincident(g133,g134)
    c: Coincident(g134,g135)
    c: Coincident(g135,g136)
    c: Coincident(g136,g137)
    c: Coincident(g137,g138)
    c: Coincident(g138,g131)
    c: Coincident(g139,g140)
    c: Coincident(g140,g141)
    c: Coincident(g141,g142)
    c: Coincident(g142,g143)
    c: Coincident(g143,g144)
    c: Coincident(g144,g145)
    c: Coincident(g145,g146)
    c: Coincident(g146,g139)
    c: Coincident(g147,g148)
    c: Coincident(g148,g149)
    c: Coincident(g149,g150)
    c: Coincident(g150,g151)
    c: Coincident(g151,g152)
    c: Coincident(g152,g153)
    c: Coincident(g153,g154)
    c: Coincident(g154,g155)
    c: Coincident(g155,g156)
    c: Coincident(g156,g157)
    c: Coincident(g157,g158)
    c: Coincident(g158,g159)
    c: Coincident(g159,g160)
    c: Coincident(g160,g161)
    c: Coincident(g161,g147)
    c: Coincident(g162,g163)
    c: Coincident(g163,g164)
    c: Coincident(g164,g165)
    c: Coincident(g165,g166)
    c: Coincident(g166,g167)
    c: Coincident(g167,g168)
    c: Coincident(g168,g169)
    c: Coincident(g169,g170)
    c: Coincident(g170,g171)
    c: Coincident(g171,g172)
    c: Coincident(g172,g173)
    c: Coincident(g173,g174)
    c: Coincident(g174,g175)
    c: Coincident(g175,g176)
    c: Coincident(g176,g177)
    c: Coincident(g177,g162)
    c: Coincident(g178,g179)
    c: Coincident(g179,g180)
    c: Coincident(g180,g181)
    c: Coincident(g181,g182)
    c: Coincident(g182,g183)
    c: Coincident(g183,g184)
    c: Coincident(g184,g185)
    c: Coincident(g185,g186)
    c: Coincident(g186,g187)
    c: Coincident(g187,g188)
    c: Coincident(g188,g189)
    c: Coincident(g189,g190)
    c: Coincident(g190,g191)
    c: Coincident(g191,g192)
    c: Coincident(g192,g193)
    c: Coincident(g193,g178)
    c: Coincident(g194,g195)
    c: Coincident(g195,g196)
    c: Coincident(g196,g197)
    c: Coincident(g197,g198)
    c: Coincident(g198,g199)
    c: Coincident(g199,g200)
    c: Coincident(g200,g201)
    c: Coincident(g201,g202)
    c: Coincident(g202,g203)
    c: Coincident(g203,g204)
    c: Coincident(g204,g205)
    c: Coincident(g205,g206)
    c: Coincident(g206,g194)
    c: Coincident(g207,g208)
    c: Coincident(g208,g209)
    c: Coincident(g209,g210)
    c: Coincident(g210,g211)
    c: Coincident(g211,g212)
    c: Coincident(g212,g213)
    c: Coincident(g213,g214)
    c: Coincident(g214,g215)
    c: Coincident(g215,g216)
    c: Coincident(g216,g217)
    c: Coincident(g217,g218)
    c: Coincident(g218,g219)
    c: Coincident(g219,g207)
    c: Coincident(g220,g221)
    c: Coincident(g221,g222)
    c: Coincident(g222,g223)
    c: Coincident(g223,g224)
    c: Coincident(g224,g225)
    c: Coincident(g225,g226)
    c: Coincident(g226,g227)
    c: Coincident(g227,g228)
    c: Coincident(g228,g220)
    c: Coincident(g229,g230)
    c: Coincident(g230,g231)
    c: Coincident(g231,g232)
    c: Coincident(g232,g233)
    c: Coincident(g233,g234)
    c: Coincident(g234,g235)
    c: Coincident(g235,g236)
    c: Coincident(g236,g229)
    c: Coincident(g237,g238)
    c: Coincident(g238,g239)
    c: Coincident(g239,g240)
    c: Coincident(g240,g241)
    c: Coincident(g241,g242)
    c: Coincident(g242,g243)
    c: Coincident(g243,g244)
    c: Coincident(g244,g237)
    c: Coincident(g245,g246)
    c: Coincident(g246,g247)
    c: Coincident(g247,g248)
    c: Coincident(g248,g249)
    c: Coincident(g249,g250)
    c: Coincident(g250,g251)
    c: Coincident(g251,g252)
    c: Coincident(g252,g253)
    c: Coincident(g253,g245)
    c: Coincident(g254,g255)
    c: Coincident(g255,g256)
    c: Coincident(g256,g257)
    c: Coincident(g257,g258)
    c: Coincident(g258,g259)
    c: Coincident(g259,g260)
    c: Coincident(g260,g261)
    c: Coincident(g261,g254)
    c: Coincident(g262,g263)
    c: Coincident(g263,g264)
    c: Coincident(g264,g265)
    c: Coincident(g265,g266)
    c: Coincident(g266,g267)
    c: Coincident(g267,g268)
    c: Coincident(g268,g269)
    c: Coincident(g269,g270)
    c: Coincident(g270,g271)
    c: Coincident(g271,g262)
    c: Coincident(g272,g273)
    c: Coincident(g273,g274)
    c: Coincident(g274,g275)
    c: Coincident(g275,g276)
    c: Coincident(g276,g277)
    c: Coincident(g277,g278)
    c: Coincident(g278,g279)
    c: Coincident(g279,g280)
    c: Coincident(g280,g272)
    c: Coincident(g281,g282)
    c: Coincident(g282,g283)
    c: Coincident(g283,g284)
    c: Coincident(g284,g285)
    c: Coincident(g285,g286)
    c: Coincident(g286,g287)
    c: Coincident(g287,g288)
    c: Coincident(g288,g289)
    c: Coincident(g289,g281)
    c: Coincident(g290,g291)
    c: Coincident(g291,g292)
    c: Coincident(g292,g293)
    c: Coincident(g293,g294)
    c: Coincident(g294,g295)
    c: Coincident(g295,g296)
    c: Coincident(g296,g297)
    c: Coincident(g297,g298)
    c: Coincident(g298,g290)
    c: Coincident(g299,g300)
    c: Coincident(g300,g301)
    c: Coincident(g301,g302)
    c: Coincident(g302,g303)
    c: Coincident(g303,g304)
    c: Coincident(g304,g305)
    c: Coincident(g305,g306)
    c: Coincident(g306,g307)
    c: Coincident(g307,g299)
    c: Coincident(g308,g309)
    c: Coincident(g309,g310)
    c: Coincident(g310,g311)
    c: Coincident(g311,g312)
    c: Coincident(g312,g313)
    c: Coincident(g313,g314)
    c: Coincident(g314,g315)
    c: Coincident(g315,g316)
    c: Coincident(g316,g317)
    c: Coincident(g317,g318)
    c: Coincident(g318,g319)
    c: Coincident(g319,g320)
    c: Coincident(g320,g321)
    c: Coincident(g321,g322)
    c: Coincident(g322,g323)
    c: Coincident(g323,g324)
    c: Coincident(g324,g308)
    c: Coincident(g325,g326)
    c: Coincident(g326,g327)
    c: Coincident(g327,g328)
    c: Coincident(g328,g329)
    c: Coincident(g329,g330)
    c: Coincident(g330,g331)
    c: Coincident(g331,g332)
    c: Coincident(g332,g333)
    c: Coincident(g333,g334)
    c: Coincident(g334,g335)
    c: Coincident(g335,g336)
    c: Coincident(g336,g337)
    c: Coincident(g337,g338)
    c: Coincident(g338,g339)
    c: Coincident(g339,g340)
    c: Coincident(g340,g341)
    c: Coincident(g341,g342)
    c: Coincident(g342,g325)
    c: Coincident(g343,g344)
    c: Coincident(g344,g345)
    c: Coincident(g345,g346)
    c: Coincident(g346,g347)
    c: Coincident(g347,g348)
    c: Coincident(g348,g349)
    c: Coincident(g349,g350)
    c: Coincident(g350,g351)
    c: Coincident(g351,g352)
    c: Coincident(g352,g353)
    c: Coincident(g353,g354)
    c: Coincident(g354,g355)
    c: Coincident(g355,g356)
    c: Coincident(g356,g357)
    c: Coincident(g357,g358)
    c: Coincident(g358,g359)
    c: Coincident(g359,g360)
    c: Coincident(g360,g361)
    c: Coincident(g361,g343)
    c: Coincident(g362,g363)
    c: Coincident(g363,g364)
    c: Coincident(g364,g365)
    c: Coincident(g365,g366)
    c: Coincident(g366,g367)
    c: Coincident(g367,g368)
    c: Coincident(g368,g369)
    c: Coincident(g369,g370)
    c: Coincident(g370,g371)
    c: Coincident(g371,g372)
    c: Coincident(g372,g373)
    c: Coincident(g373,g374)
    c: Coincident(g374,g375)
    c: Coincident(g375,g376)
    c: Coincident(g376,g377)
    c: Coincident(g377,g378)
    c: Coincident(g378,g379)
    c: Coincident(g379,g380)
    c: Coincident(g380,g362)
    c: Coincident(g381,g382)
    c: Coincident(g382,g383)
    c: Coincident(g383,g384)
    c: Coincident(g384,g385)
    c: Coincident(g385,g386)
    c: Coincident(g386,g387)
    c: Coincident(g387,g388)
    c: Coincident(g388,g389)
    c: Coincident(g389,g390)
    c: Coincident(g390,g391)
    c: Coincident(g391,g392)
    c: Coincident(g392,g393)
    c: Coincident(g393,g394)
    c: Coincident(g394,g395)
    c: Coincident(g395,g396)
    c: Coincident(g396,g397)
    c: Coincident(g397,g398)
    c: Coincident(g398,g399)
    c: Coincident(g399,g381)
    c: Coincident(g400,g401)
    c: Coincident(g401,g402)
    c: Coincident(g402,g403)
    c: Coincident(g403,g404)
    c: Coincident(g404,g405)
    c: Coincident(g405,g406)
    c: Coincident(g406,g400)
    c: Coincident(g407,g408)
    c: Coincident(g408,g409)
    c: Coincident(g409,g410)
    c: Coincident(g410,g411)
    c: Coincident(g411,g412)
    c: Coincident(g412,g407)
    c: Coincident(g413,g414)
    c: Coincident(g414,g415)
    c: Coincident(g415,g416)
    c: Coincident(g416,g417)
    c: Coincident(g417,g418)
    c: Coincident(g418,g419)
    c: Coincident(g419,g413)
    c: Coincident(g420,g421)
    c: Coincident(g421,g422)
    c: Coincident(g422,g423)
    c: Coincident(g423,g424)
    c: Coincident(g424,g425)
    c: Coincident(g425,g426)
    c: Coincident(g426,g420)
    c: Coincident(g427,g428)
    c: Coincident(g428,g429)
    c: Coincident(g429,g430)
    c: Coincident(g430,g431)
    c: Coincident(g431,g432)
    c: Coincident(g432,g433)
    c: Coincident(g433,g434)
    c: Coincident(g434,g435)
    c: Coincident(g435,g427)
    c: Coincident(g436,g437)
    c: Coincident(g437,g438)
    c: Coincident(g438,g439)
    c: Coincident(g439,g440)
    c: Coincident(g440,g441)
    c: Coincident(g441,g442)
    c: Coincident(g442,g443)
    c: Coincident(g443,g436)
    c: Coincident(g444,g445)
    c: Coincident(g445,g446)
    c: Coincident(g446,g447)
    c: Coincident(g447,g448)
    c: Coincident(g448,g449)
    c: Coincident(g449,g450)
    c: Coincident(g450,g451)
    c: Coincident(g451,g444)
    c: Coincident(g452,g453)
    c: Coincident(g453,g454)
    c: Coincident(g454,g455)
    c: Coincident(g455,g456)
    c: Coincident(g456,g457)
    c: Coincident(g457,g458)
    c: Coincident(g458,g459)
    c: Coincident(g459,g452)
    c: Coincident(g460,g461)
    c: Coincident(g461,g462)
    c: Coincident(g462,g463)
    c: Coincident(g463,g464)
    c: Coincident(g464,g465)
    c: Coincident(g465,g466)
    c: Coincident(g466,g467)
    c: Coincident(g467,g460)
    c: Coincident(g468,g469)
    c: Coincident(g469,g470)
    c: Coincident(g470,g471)
    c: Coincident(g471,g472)
    c: Coincident(g472,g473)
    c: Coincident(g473,g474)
    c: Coincident(g474,g475)
    c: Coincident(g475,g468)
    c: Coincident(g476,g477)
    c: Coincident(g477,g478)
    c: Coincident(g478,g479)
    c: Coincident(g479,g480)
    c: Coincident(g480,g476)
    c: Coincident(g481,g482)
    c: Coincident(g482,g483)
    c: Coincident(g483,g484)
    c: Coincident(g484,g485)
    c: Coincident(g485,g486)
    c: Coincident(g486,g481)
    c: Coincident(g487,g488)
    c: Coincident(g488,g489)
    c: Coincident(g489,g490)
    c: Coincident(g490,g491)
    c: Coincident(g491,g492)
    c: Coincident(g492,g493)
    c: Coincident(g493,g487)
    c: Coincident(g494,g495)
    c: Coincident(g495,g496)
    c: Coincident(g496,g497)
    c: Coincident(g497,g498)
    c: Coincident(g498,g499)
    c: Coincident(g499,g494)
    c: Coincident(g500,g501)
    c: Coincident(g501,g502)
    c: Coincident(g502,g503)
    c: Coincident(g503,g504)
    c: Coincident(g504,g505)
    c: Coincident(g505,g506)
    c: Coincident(g506,g507)
    c: Coincident(g507,g500)
    c: Coincident(g508,g509)
    c: Coincident(g509,g510)
    c: Coincident(g510,g511)
    c: Coincident(g511,g512)
    c: Coincident(g512,g513)
    c: Coincident(g513,g514)
    c: Coincident(g514,g515)
    c: Coincident(g515,g508)
    c: Coincident(g516,g517)
    c: Coincident(g517,g518)
    c: Coincident(g518,g519)
    c: Coincident(g519,g520)
    c: Coincident(g520,g521)
    c: Coincident(g521,g522)
    c: Coincident(g522,g523)
    c: Coincident(g523,g524)
    c: Coincident(g524,g516)
    c: Coincident(g525,g526)
    c: Coincident(g526,g527)
    c: Coincident(g527,g528)
    c: Coincident(g528,g529)
    c: Coincident(g529,g530)
    c: Coincident(g530,g531)
    c: Coincident(g531,g532)
    c: Coincident(g532,g533)
    c: Coincident(g533,g534)
    c: Coincident(g534,g525)
    c: Coincident(g535,g536)
    c: Coincident(g536,g537)
    c: Coincident(g537,g538)
    c: Coincident(g538,g539)
    c: Coincident(g539,g540)
    c: Coincident(g540,g541)
    c: Coincident(g541,g542)
    c: Coincident(g542,g543)
    c: Coincident(g543,g535)
    c: Coincident(g544,g545)
    c: Coincident(g545,g546)
    c: Coincident(g546,g547)
    c: Coincident(g547,g548)
    c: Coincident(g548,g549)
    c: Coincident(g549,g550)
    c: Coincident(g550,g544)
    c: Coincident(g551,g552)
    c: Coincident(g552,g553)
    c: Coincident(g553,g554)
    c: Coincident(g554,g555)
    c: Coincident(g555,g556)
    c: Coincident(g556,g551)
FEATURE [PartDesign::Pad] Pad
  Direction = (0,0,1)
  Length = 5
  Length2 = 10
  Profile = -> Sketch
  ReferenceAxis = -> Sketch [N_Axis]
  Suppressed = false
  Type = 0
FEATURE [PartDesign::Body] Body
  AllowCompound = false
  Group = -> [Sketch,Pad]
  Origin = -> Origin
  Placement = pos=(0,170,0) rot=(0,0,1;0rad)
  Tip = -> Pad
FEATURE [Part::Box] Box  label="Cube"
  AttacherType = Attacher::AttachEngine3D
  Height = 5
  Length = 10
  Placement = pos=(1,-9,0) rot=(0,0,1;0rad)
  Width = 30
FEATURE [Part::Box] Box001  label="Cube001"
  AttacherType = Attacher::AttachEngine3D
  Height = 5
  Length = 10
  Placement = pos=(107,-9,0) rot=(0,0,1;0rad)
  Width = 30
FEATURE [Part::MultiFuse] Fusion
  Shapes = -> [Body,Box,Box001]
